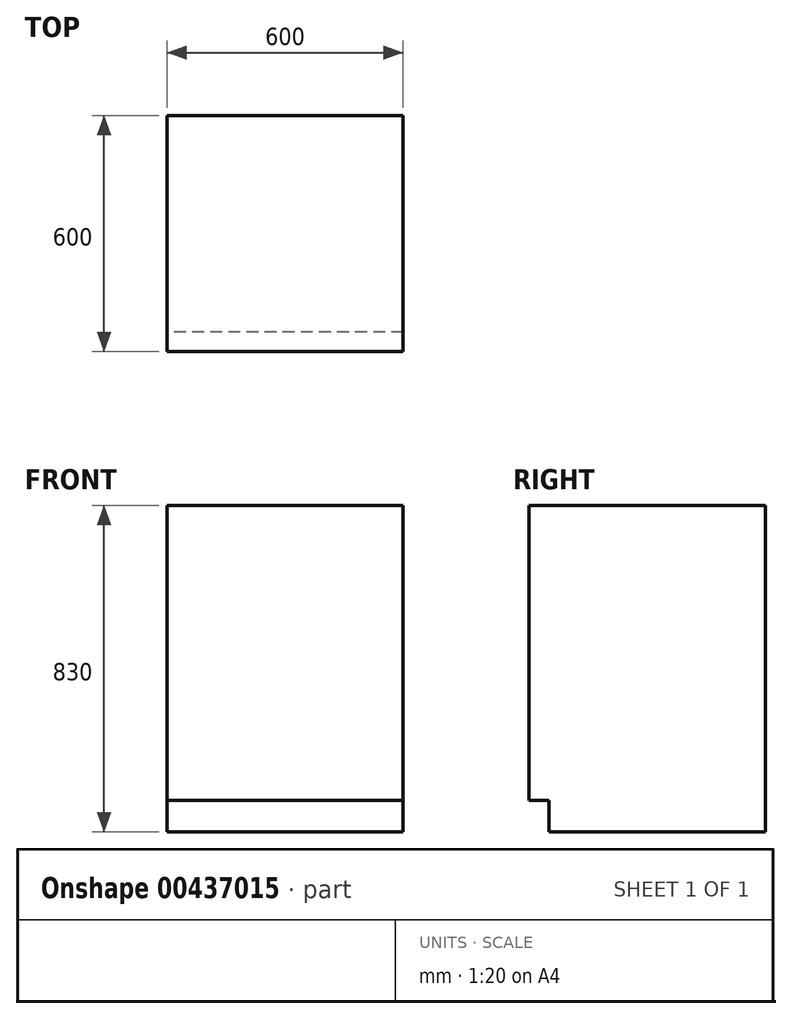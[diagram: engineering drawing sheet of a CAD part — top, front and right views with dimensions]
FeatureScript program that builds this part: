
annotation { "Feature Type Name" : "Feature", "Feature Type Description" : "" }
export const myFeature = defineFeature(function(context is Context, id is Id, definition is map)
    precondition{}
    {
        {
            var Q0;
            Q0=qCreatedBy(makeId("Right.planeOp"),FACE);
            var sketch = newSketch(context, id + "F0", { "sketchPlane" : qUnion([Q0])});
            skLineSegment(sketch, "E0.bottom", {"start": v(0, 0) * mm, "end": v(-550, 0) * mm});
            skLineSegment(sketch, "E0.top", {"start": v(0, 830) * mm, "end": v(-600, 830) * mm});
            skLineSegment(sketch, "E0.left", {"start": v(0, 0) * mm, "end": v(0, 830) * mm});
            skLineSegment(sketch, "E0.right", {"start": v(-600, 80) * mm, "end": v(-600, 830) * mm});
            skLineSegment(sketch, "E1.top", {"start": v(-600, 80) * mm, "end": v(-550, 80) * mm});
            skLineSegment(sketch, "E1.right", {"start": v(-550, 0) * mm, "end": v(-550, 80) * mm});
            skSolve(sketch);
        }
        {
            var Q0;
            Q0=qSketchRegion(id+"F0",true);
            extrude(context, id + "F1", {"entities" : qUnion([Q0]), "depth" : 600 * mm});
        }
    });
